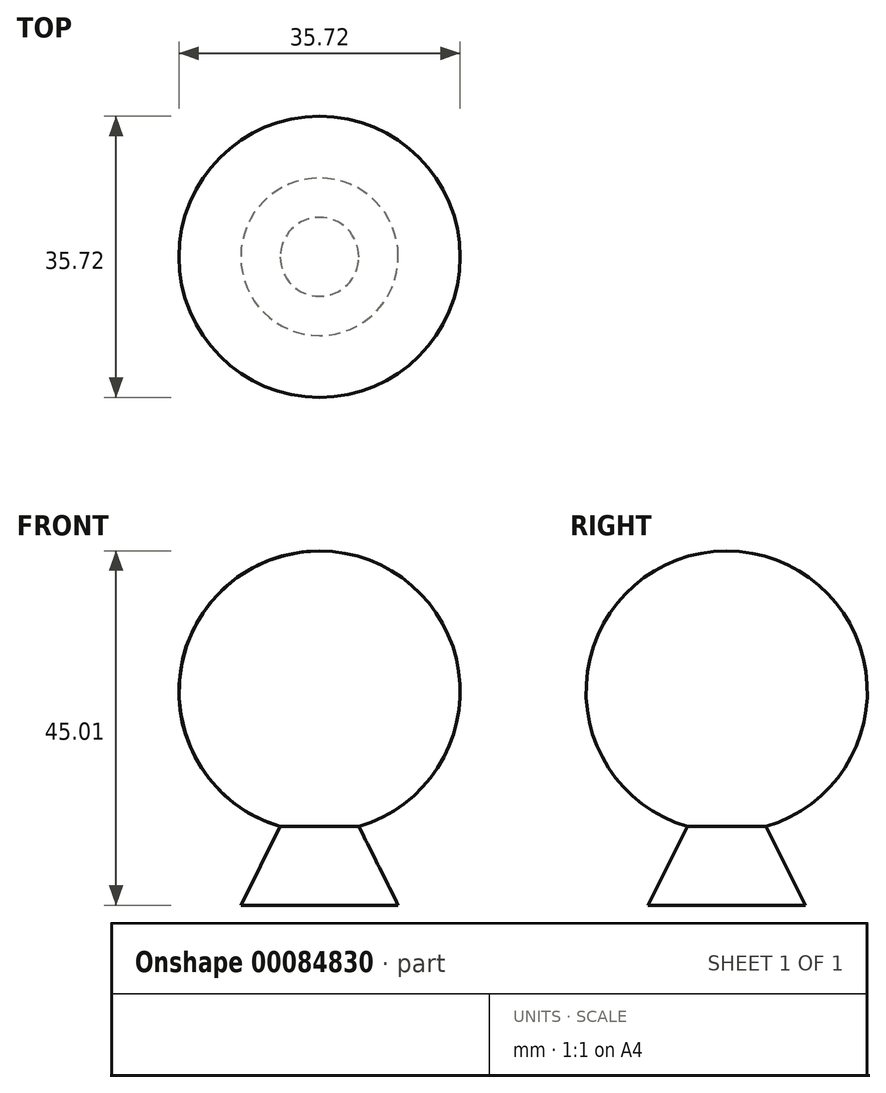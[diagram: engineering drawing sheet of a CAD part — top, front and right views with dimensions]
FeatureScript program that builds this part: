
annotation { "Feature Type Name" : "Feature", "Feature Type Description" : "" }
export const myFeature = defineFeature(function(context is Context, id is Id, definition is map)
    precondition{}
    {
        {
            var Q0;
            Q0=qCreatedBy(makeId("Front.planeOp"),FACE);
            var sketch = newSketch(context, id + "F0", { "sketchPlane" : qUnion([Q0])});
            skArc(sketch, "E0", {"start": v(0, 0) * mm, "mid": v(17.86, 17.86) * mm, "end": v(0, 35.72) * mm});
            skLineSegment(sketch, "E1", {"start": v(0, 35.72) * mm, "end": v(0, 0) * mm});
            skSolve(sketch);
        }
        {
            var Q0;
            Q0=makeQuery(id+"F0.imprint","IMPRINT",FACE,{"disambiguationData":[TD([[makeQuery(id+"F0.imprint","IMPRINT",EDGE,{"derivedFrom":sQuery(id+"F0.wireOp",EDGE,"E0")}),1.0]])]});
            var Q1;
            Q1=sQuery(id+"F0.wireOp",EDGE,"E1");
            revolve(context, id + "F1", {"entities" : qUnion([Q0]), "axis" : qUnion([Q1]), "revolveType" : RevolveType.FULL});
        }
        {
            var Q0;
            Q0=qCreatedBy(makeId("Front.planeOp"),FACE);
            var sketch = newSketch(context, id + "F2", { "sketchPlane" : qUnion([Q0])});
            skLineSegment(sketch, "E2", {"start": v(5, 0.71) * mm, "end": v(10, -9.29) * mm});
            skLineSegment(sketch, "E3", {"start": v(10, -9.29) * mm, "end": v(-10, -9.29) * mm});
            skLineSegment(sketch, "E4", {"start": v(-10, -9.29) * mm, "end": v(-5, 0.71) * mm});
            skLineSegment(sketch, "E5", {"start": v(-5, 0.71) * mm, "end": v(5, 0.71) * mm});
            skPoint(sketch, "E6", {"position": v(0, 0.71) * mm});
            skPoint(sketch, "E7", {"position": v(0, -9.29) * mm});
            skLineSegment(sketch, "E8", {"start": v(0, 0.71) * mm, "end": v(0, -9.29) * mm});
            skSolve(sketch);
        }
        {
            var Q0;
            {var subQ0=sQuery(id+"F2.wireOp",EDGE,"E2");Q0=makeQuery(id+"F2.imprint","IMPRINT",FACE,{"disambiguationData":[TD([[makeQuery(id+"F2.imprint","IMPRINT",EDGE,{"derivedFrom":subQ0}),-1.0]])]});}
            var Q1;
            Q1=sQuery(id+"F2.wireOp",EDGE,"E8");
            revolve(context, id + "F3", {"operationType" : NewBodyOperationType.ADD, "entities" : qUnion([Q0]), "axis" : qUnion([Q1]), "revolveType" : RevolveType.FULL});
        }
    });
